# Revit family: ТвінФреш Стайл_Eng
name_source: partatom
category: Mechanical Equipment
units: mm (PartAtom-declared; Revit-internal decimal feet)

## family parameters
Always vertical = Yes
Classification = None
Cut with Voids When Loaded = Yes
Part Type = Normal
Room Calculation Point = No
Round Connector Dimension = Use Diameter
Shared = No
Work Plane-Based = No

## types (4) — shared parameters
00_20_Manufacturer = Vents
00_20_Name = Ventilator
B1 = 186 mm  [stored 0.610236 ft]
Casing Material = Plastic, opaque, white
Filter = G3
Frequency = 50 Hz
Height = 305 mm  [stored 1.00066 ft]
L2 = 86 mm  [stored 0.282152 ft]
Lid = No
Load Classification = HVAC
Maintenance zone material = <By Category>
Manufacturer = Vents
Number of Fase = 1
URL = https://ventilation-system.com
Voltage = 230 V
Weight = 5.00 kg
Width = 280 mm  [stored 0.918635 ft]
zero-valued in all types: Default Elevation

## per-type parameters (varying)
| type | Amperage | B | D | Dy | L | Length | Maximum Air Flow | Power | Sound pressure level at 3 m distance | b | b1 | l1 | l2 | l3 |
| TwinFresh Style | 0.060 A | 240 mm  [stored 0.787402 ft] | 160 mm  [stored 0.524934 ft] | 155 mm  [stored 0.50853 ft] | 300 mm | 432 mm  [stored 1.41732 ft] | 50.0 m³/h | 6 W | 26 dBA | 180 mm  [stored 0.590551 ft] | 200 mm  [stored 0.656168 ft] | 150 mm | 156 mm  [stored 0.511811 ft] | 145 mm  [stored 0.475722 ft] |
| TwinFresh Style WiFi | 0.060 A | 240 mm  [stored 0.787402 ft] | 160 mm  [stored 0.524934 ft] | 155 mm  [stored 0.50853 ft] | 300 mm | 432 mm  [stored 1.41732 ft] | 50.0 m³/h | 6 W | 26 dBA | 180 mm  [stored 0.590551 ft] | 200 mm  [stored 0.656168 ft] | 150 mm | 156 mm  [stored 0.511811 ft] | 145 mm  [stored 0.475722 ft] |
| TwinFresh Style mini | 0.050 A | 280 mm  [stored 0.918635 ft] | 100 mm  [stored 0.328084 ft] | 95 mm | 200 mm  [stored 0.656168 ft] | 332 mm | 30.0 m³/h | 4 W | 31 dBA | 220 mm  [stored 0.721785 ft] | 240 mm  [stored 0.787402 ft] | 100 mm  [stored 0.328084 ft] | 106 mm | 95 mm |
| TwinFresh Style Wi-Fi mini | 0.050 A | 240 mm  [stored 0.787402 ft] | 100 mm  [stored 0.328084 ft] | 95 mm | 200 mm  [stored 0.656168 ft] | 332 mm | 30.0 m³/h | 4 W | 31 dBA | 180 mm  [stored 0.590551 ft] | 200 mm  [stored 0.656168 ft] | 100 mm  [stored 0.328084 ft] | 106 mm | 95 mm |

note: column(s) folded — value = type name in every type: 00_20_Type

note: [stored X ft] marks values corroborated as IEEE doubles in the binary element streams (Revit-internal decimal feet)
